# Revit family: ROSENBERG_KBAD_450-500
name_source: partatom
category: Wyposażenie mechaniczne
revit_build: Autodesk Revit MEP 2016 (Build: 20150220_1215(x64)
units: mm (PartAtom-declared; Revit-internal decimal feet)

## family parameters
Numer OmniClass = 23.75.00.00
Oparty na płaszczyźnie roboczej = Tak
Punkt obliczania pomieszczeń = Nie
Tnij formami wycięć po wczytaniu = Nie
Typ części = Normalny
Tytuł OmniClass = Climate Control (HVAC)
Współdzielony = Nie
Wymiar okrągłego złącza = Użyj średnicy
Zawsze pionowo = Tak

## types (2) — shared parameters
1.param.H.podstawa = 29 mm  [stored 0.0951444 ft]
1.param.W.podstawa = 38 mm  [stored 0.124672 ft]
1.param.dł.podsatawa = 800 mm  [stored 2.62467 ft]
1.param.odusnięcie.urządzenie.front = 35 mm  [stored 0.114829 ft]
2.param.H.urządzenia = 800 mm  [stored 2.62467 ft]
2.param.W.urządzenia = 900 mm  [stored 2.95276 ft]
2.param.szer.klapa = 60 mm  [stored 0.19685 ft]
2.param.szer.urządzenie = 415 mm  [stored 1.36155 ft]
3.param.L.tyl.went = 603 mm
4.param.h.wlot = 450 mm  [stored 1.47638 ft]
4.param.odsunięcie.wlot = 511 mm
5.param.h.wylot = 45 mm
5.param.odsunięcie.wylot = 300 mm
5.param.os.went.wyw = 178 mm
Charakterystyka pracy = https://rosenberg.pl
Częstotliwość pracy = 50 Hz
Domyślna rzędna = 1219 mm
Klasa szczelności = IP54
Masa = 92.00 kg
Materiał = <Wg kategorii>
Napięcie znamionowe = 400 V
Opis = Wentylator do okapów kuchennych
Producent = Rosenberg
Prąd znamionowy = 2 A
Typ zasilania = 3
URL = https://rosenberg.pl
param.L.otwor = 143 mm
param.lb.otwor = 10
param.odl.rączka = 55 mm
param.otw.wew = 300 mm
param.otwory. = 5 mm  [stored 0.0164042 ft]
param.puszka.przył = 140 mm
param.void = 440 mm  [stored 1.44357 ft]
Średnica przyłącza = 450 mm  [stored 1.47638 ft]

## per-type parameters (varying)
| type | Moc znamionowa | Numer katalogowy | param.h.450 |
| KBAD 500-4SW.138 | 1550 W | B21-50014 | 260 mm  [stored 0.853018 ft] |
| KBAD 450-4SW.138 | 910 W | B21-45016 | 280 mm |

note: column(s) folded — value = type name in every type: Model

note: [stored X ft] marks values corroborated as IEEE doubles in the binary element streams (Revit-internal decimal feet)

## geometry (parser evidence)
native form markers: Blend x4, Sweep x5
no freeform markers — native parametric forms only
